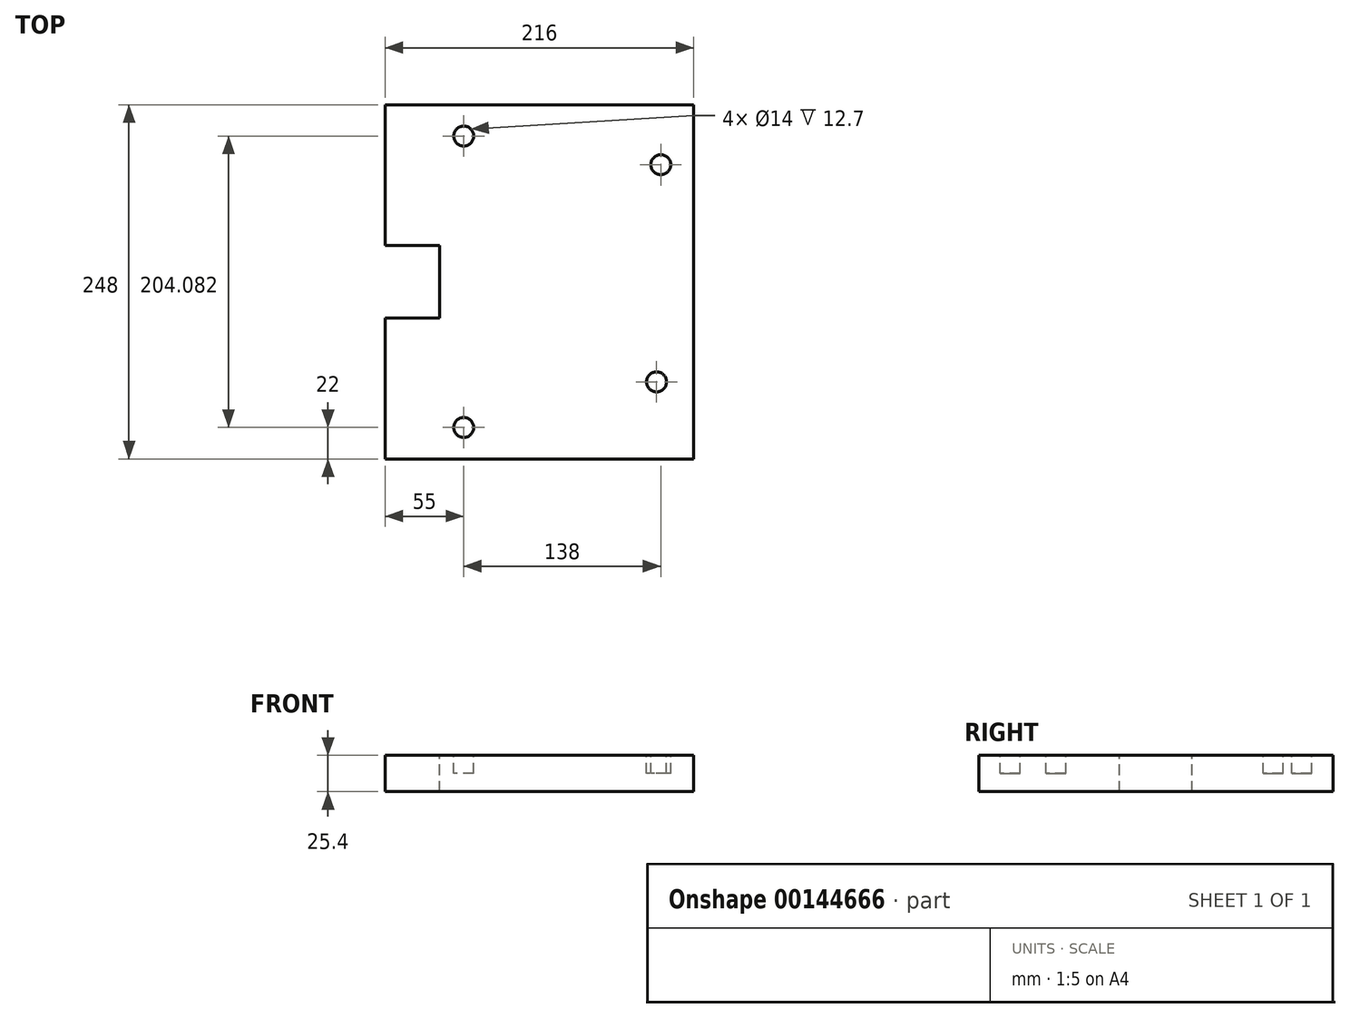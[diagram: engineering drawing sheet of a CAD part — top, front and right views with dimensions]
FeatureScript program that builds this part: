
annotation { "Feature Type Name" : "Feature", "Feature Type Description" : "" }
export const myFeature = defineFeature(function(context is Context, id is Id, definition is map)
    precondition{}
    {
        {
            var Q0;
            Q0=qCreatedBy(makeId("Front.planeOp"),FACE);
            var sketch = newSketch(context, id + "F0", { "sketchPlane" : qUnion([Q0])});
            skLineSegment(sketch, "E0.bottom", {"start": v(0, 0) * mm, "end": v(-216, 0) * mm});
            skLineSegment(sketch, "E0.top", {"start": v(0, 25.4) * mm, "end": v(-216, 25.4) * mm});
            skLineSegment(sketch, "E0.left", {"start": v(0, 0) * mm, "end": v(0, 25.4) * mm});
            skLineSegment(sketch, "E0.right", {"start": v(-216, 0) * mm, "end": v(-216, 25.4) * mm});
            skSolve(sketch);
        }
        {
            var Q0;
            Q0=makeQuery(id+"F0.imprint","IMPRINT",FACE,{"disambiguationData":[TD([[makeQuery(id+"F0.imprint","IMPRINT",EDGE,{"derivedFrom":sQuery(id+"F0.wireOp",EDGE,"E0.bottom")}),-1.0]])]});
            extrude(context, id + "F1", {"entities" : qUnion([Q0]), "oppositeDirection" : true, "depth" : 248 * mm});
        }
        {
            var Q0;
            Q0=makeQuery(id+"F1.opExtrude","SWEPT_FACE",FACE,{"disambiguationData":[OSD([sQuery(id+"F0.wireOp",EDGE,"E0.top")])]});
            var sketch = newSketch(context, id + "F2", { "sketchPlane" : qUnion([Q0])});
            skCircle(sketch, "E1", {"center": v(-23, 206) * mm, "radius": 7 * mm});
            skCircle(sketch, "E2", {"center": v(-26, 53.95) * mm, "radius": 7 * mm});
            skCircle(sketch, "E3", {"center": v(-161, 226.08) * mm, "radius": 7 * mm});
            skCircle(sketch, "E4", {"center": v(-161, 22) * mm, "radius": 7 * mm});
            skSolve(sketch);
        }
        {
            var Q0;
            Q0=makeQuery(id+"F2.imprint","IMPRINT",FACE,{"disambiguationData":[TD([[makeQuery(id+"F2.imprint","IMPRINT",EDGE,{"derivedFrom":sQuery(id+"F2.wireOp",EDGE,"E3")}),1.0]])]});
            var Q1;
            Q1=makeQuery(id+"F2.imprint","IMPRINT",FACE,{"disambiguationData":[TD([[makeQuery(id+"F2.imprint","IMPRINT",EDGE,{"derivedFrom":sQuery(id+"F2.wireOp",EDGE,"E4")}),1.0]])]});
            var Q2;
            Q2=makeQuery(id+"F2.imprint","IMPRINT",FACE,{"disambiguationData":[TD([[makeQuery(id+"F2.imprint","IMPRINT",EDGE,{"derivedFrom":sQuery(id+"F2.wireOp",EDGE,"E1")}),1.0]])]});
            var Q3;
            Q3=makeQuery(id+"F2.imprint","IMPRINT",FACE,{"disambiguationData":[TD([[makeQuery(id+"F2.imprint","IMPRINT",EDGE,{"derivedFrom":sQuery(id+"F2.wireOp",EDGE,"E2")}),1.0]])]});
            extrude(context, id + "F3", {"entities" : qUnion([Q0, Q1, Q2, Q3]), "operationType" : NewBodyOperationType.REMOVE, "oppositeDirection" : true, "depth" : 12.7 * mm});
        }
        {
            var Q0;
            Q0=makeQuery(id+"F1.opExtrude","SWEPT_FACE",FACE,{"disambiguationData":[OSD([sQuery(id+"F0.wireOp",EDGE,"E0.top")])]});
            var sketch = newSketch(context, id + "F4", { "sketchPlane" : qUnion([Q0])});
            skLineSegment(sketch, "E5", {"start": v(-216, 248) * mm, "end": v(-216, 149.4) * mm, "construction": true});
            skLineSegment(sketch, "E6", {"start": v(-216, 0) * mm, "end": v(-216, 98.6) * mm, "construction": true});
            skLineSegment(sketch, "E7.bottom", {"start": v(-216, 149.4) * mm, "end": v(-178, 149.4) * mm});
            skLineSegment(sketch, "E7.top", {"start": v(-216, 98.6) * mm, "end": v(-178, 98.6) * mm});
            skLineSegment(sketch, "E7.left", {"start": v(-216, 149.4) * mm, "end": v(-216, 98.6) * mm});
            skLineSegment(sketch, "E7.right", {"start": v(-178, 149.4) * mm, "end": v(-178, 98.6) * mm});
            skSolve(sketch);
        }
        {
            var Q0;
            Q0=makeQuery(id+"F4.imprint","IMPRINT",FACE,{"disambiguationData":[TD([[makeQuery(id+"F4.imprint","IMPRINT",EDGE,{"derivedFrom":sQuery(id+"F4.wireOp",EDGE,"E7.bottom")}),-1.0]])]});
            var Q1;
            Q1=makeQuery(id+"F4.imprint","IMPRINT",FACE,{"disambiguationData":[TD([[makeQuery(id+"F4.imprint","IMPRINT",EDGE,{"derivedFrom":makeQuery(id+"F3.boolean.opBoolean","COPY",EDGE,{"derivedFrom":makeQuery(id+"F3.opExtrude","CAP_EDGE",EDGE,{"disambiguationData":[OSD([sQuery(id+"F2.wireOp",EDGE,"E2")])],"isStart":true})})}),1.0]])]});
            var Q2;
            Q2=makeQuery(id+"F1.opExtrude","SWEPT_FACE",FACE,{"disambiguationData":[OSD([sQuery(id+"F0.wireOp",EDGE,"E0.bottom")])]});
            extrude(context, id + "F5", {"entities" : qUnion([Q0, Q1]), "operationType" : NewBodyOperationType.REMOVE, "endBound" : BoundingType.UP_TO_SURFACE, "oppositeDirection" : true, "endBoundEntityFace" : qUnion([Q2]), "depth" : 25.4 * mm});
        }
    });
